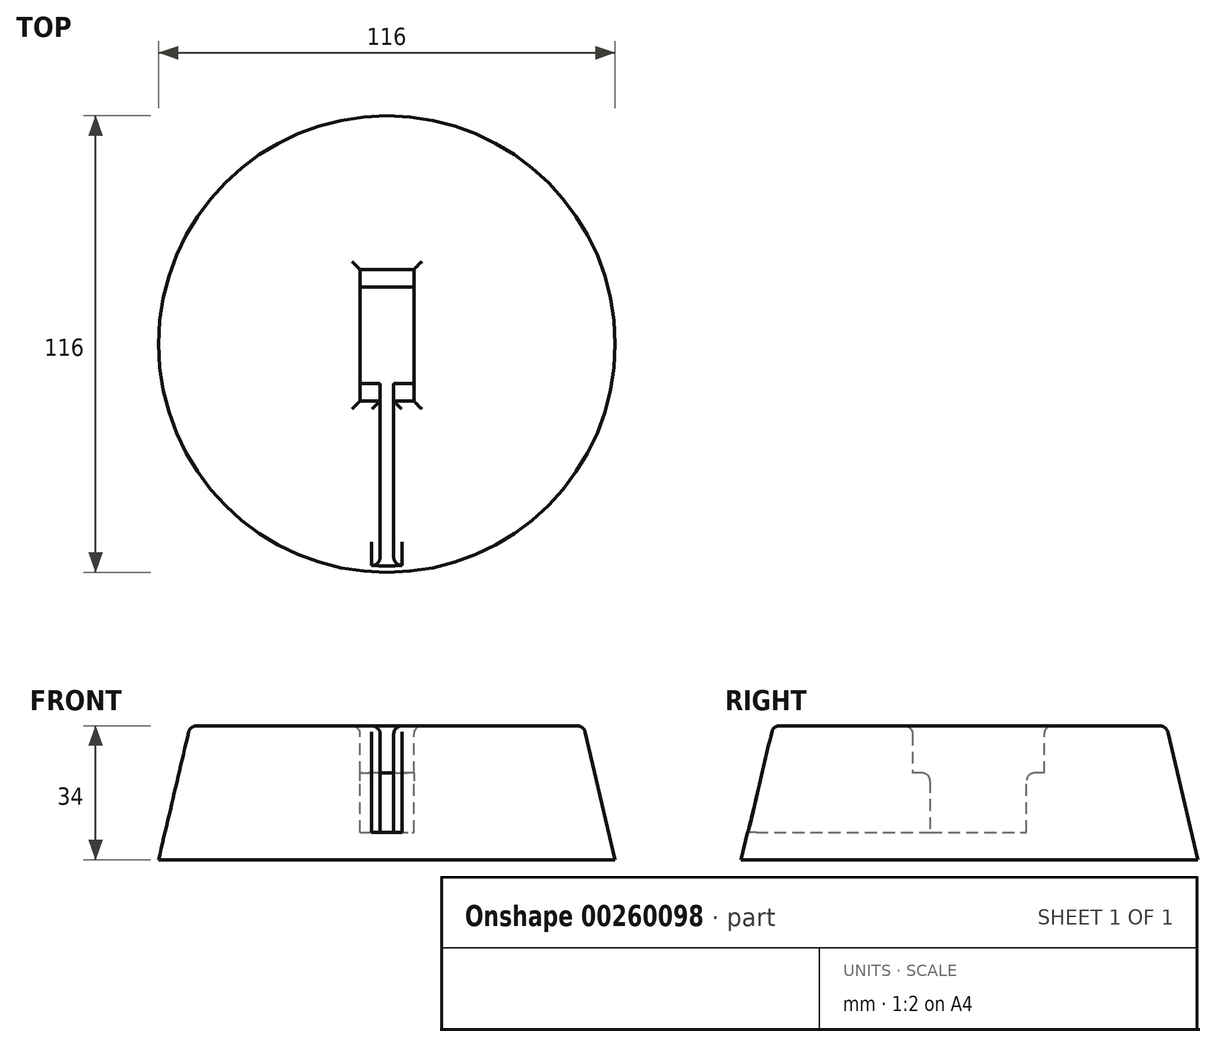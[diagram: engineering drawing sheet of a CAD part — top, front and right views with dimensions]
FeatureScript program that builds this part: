
annotation { "Feature Type Name" : "Feature", "Feature Type Description" : "" }
export const myFeature = defineFeature(function(context is Context, id is Id, definition is map)
    precondition{}
    {
        {
            var Q0;
            Q0=qCreatedBy(makeId("Top.planeOp"),FACE);
            var sketch = newSketch(context, id + "F0", { "sketchPlane" : qUnion([Q0])});
            skCircle(sketch, "E0", {"center": v(0, 0) * mm, "radius": 50 * mm});
            skSolve(sketch);
        }
        {
            var Q0;
            Q0 = qSketchRegion(id + "F0", true);
            extrude(context, id + "F1", {"entities" : qUnion([Q0]), "depth" : 34 * mm});
        }
        {
            var Q0;
            Q0=makeQuery(id+"F1.opExtrude","CAP_FACE",FACE,{"disambiguationData":[OSD([sQuery(id+"F0.wireOp",EDGE,"E0")])],"isStart":true});
            var sketch = newSketch(context, id + "F2", { "sketchPlane" : qUnion([Q0])});
            skCircle(sketch, "E1.0", {"center": v(0, 0) * mm, "radius": 58 * mm});
            skSolve(sketch);
        }
        {
            var Q0;
            Q0=makeQuery(id+"F1.opExtrude","CAP_FACE",FACE,{"disambiguationData":[OSD([sQuery(id+"F0.wireOp",EDGE,"E0")])],"isStart":false});
            var sketch = newSketch(context, id + "F3", { "sketchPlane" : qUnion([Q0])});
            skCircle(sketch, "E2.0.0", {"center": v(0, 0) * mm, "radius": 50 * mm});
            skSolve(sketch);
        }
        {
            var Q1;
            Q1=makeQuery(id+"F3.imprint","IMPRINT",FACE,{"disambiguationData":[TD([[makeQuery(id+"F3.imprint","IMPRINT",EDGE,{"derivedFrom":sQuery(id+"F3.wireOp",EDGE,"E2.0.0")}),1.0]])]});
            var Q2;
            Q2 = qSketchRegion(id + "F2", true);
            loft(context, id + "F4", {"operationType" : NewBodyOperationType.ADD, "sheetProfilesArray" : [{ "sheetProfileEntities" : qUnion([Q1]) }, { "sheetProfileEntities" : qUnion([Q2]) }]});
        }
        {
            var Q0;
            Q0=makeQuery(id+"F1.opExtrude","CAP_FACE",FACE,{"disambiguationData":[OSD([sQuery(id+"F0.wireOp",EDGE,"E0")])],"isStart":false});
            var sketch = newSketch(context, id + "F5", { "sketchPlane" : qUnion([Q0])});
            skLineSegment(sketch, "E3.bottom", {"start": v(-6.87, -10) * mm, "end": v(6.88, -10) * mm});
            skLineSegment(sketch, "E3.top", {"start": v(-6.88, 14.5) * mm, "end": v(6.87, 14.5) * mm});
            skLineSegment(sketch, "E3.left", {"start": v(-6.87, -10) * mm, "end": v(-6.88, 14.5) * mm});
            skLineSegment(sketch, "E3.right", {"start": v(6.88, -10) * mm, "end": v(6.87, 14.5) * mm});
            skSolve(sketch);
        }
        {
            var Q0;
            Q0 = qSketchRegion(id + "F5", true);
            extrude(context, id + "F6", {"entities" : qUnion([Q0]), "operationType" : NewBodyOperationType.REMOVE, "oppositeDirection" : true, "depth" : 27 * mm});
        }
        {
            var Q0;
            Q0=makeQuery(id+"F1.opExtrude","CAP_FACE",FACE,{"disambiguationData":[OSD([sQuery(id+"F0.wireOp",EDGE,"E0")])],"isStart":false});
            var sketch = newSketch(context, id + "F7", { "sketchPlane" : qUnion([Q0])});
            skPoint(sketch, "E4.oppositeSnap0", {"position": v(6.88, 2.25) * mm});
            skLineSegment(sketch, "E4.bottom", {"start": v(-6.88, 19) * mm, "end": v(6.88, 19) * mm});
            skLineSegment(sketch, "E4.top", {"start": v(-6.87, -14.5) * mm, "end": v(6.88, -14.5) * mm});
            skLineSegment(sketch, "E4.left", {"start": v(-6.88, 19) * mm, "end": v(-6.87, -14.5) * mm});
            skLineSegment(sketch, "E4.right", {"start": v(6.88, 19) * mm, "end": v(6.88, -14.5) * mm});
            skSolve(sketch);
        }
        {
            var Q0;
            Q0 = qSketchRegion(id + "F7", true);
            extrude(context, id + "F8", {"entities" : qUnion([Q0]), "operationType" : NewBodyOperationType.REMOVE, "oppositeDirection" : true, "depth" : 12 * mm});
        }
        {
            var Q0;
            Q0=makeQuery(id+"F1.opExtrude","CAP_FACE",FACE,{"disambiguationData":[OSD([sQuery(id+"F0.wireOp",EDGE,"E0")])],"isStart":false});
            var sketch = newSketch(context, id + "F9", { "sketchPlane" : qUnion([Q0])});
            skLineSegment(sketch, "E5.bottom", {"start": v(-1.75, -6.6) * mm, "end": v(1.75, -6.6) * mm});
            skLineSegment(sketch, "E5.top", {"start": v(-1.75, -69.31) * mm, "end": v(1.75, -69.31) * mm});
            skLineSegment(sketch, "E5.left", {"start": v(-1.75, -6.6) * mm, "end": v(-1.75, -69.31) * mm});
            skLineSegment(sketch, "E5.right", {"start": v(1.75, -6.6) * mm, "end": v(1.75, -69.31) * mm});
            skLineSegment(sketch, "E6", {"start": v(0, 50) * mm, "end": v(0, -50) * mm, "construction": true});
            skSolve(sketch);
        }
        {
            var Q0;
            Q0 = qSketchRegion(id + "F9", true);
            var Q1;
            Q1=makeQuery(id+"F6.boolean.opBoolean","COPY",FACE,{"derivedFrom":makeQuery(id+"F6.opExtrude","CAP_FACE",FACE,{"disambiguationData":[OSD([sQuery(id+"F5.wireOp",EDGE,"E3.bottom"),sQuery(id+"F5.wireOp",EDGE,"E3.top"),sQuery(id+"F5.wireOp",EDGE,"E3.left"),sQuery(id+"F5.wireOp",EDGE,"E3.right")])],"isStart":false})});
            extrude(context, id + "F10", {"entities" : qUnion([Q0]), "operationType" : NewBodyOperationType.REMOVE, "endBound" : BoundingType.UP_TO_SURFACE, "oppositeDirection" : true, "endBoundEntityFace" : qUnion([Q1]), "depth" : 25 * mm});
        }
        {
            var Q0;
            Q0=makeQuery(id+"F8.boolean.opBoolean","COPY",EDGE,{"derivedFrom":makeQuery(id+"F8.opExtrude","CAP_EDGE",EDGE,{"disambiguationData":[OSD([sQuery(id+"F7.wireOp",EDGE,"HFsGuh67-IHWy-x5wL-GzuI-69m3aBAS32or.bottom")])],"isStart":true})});
            var Q1;
            Q1=makeQuery(id+"F8.boolean.opBoolean","MERGE",EDGE,{"derivedFrom":[makeQuery(id+"F6.boolean.opBoolean","COPY",EDGE,{"derivedFrom":makeQuery(id+"F6.opExtrude","CAP_EDGE",EDGE,{"disambiguationData":[OSD([sQuery(id+"F5.wireOp",EDGE,"IrSC4I5D-AX9H-FrcX-Zehj-UdF8axFLpcCN.left")])],"isStart":true})}),makeQuery(id+"F8.opExtrude","CAP_EDGE",EDGE,{"disambiguationData":[OSD([sQuery(id+"F7.wireOp",EDGE,"HFsGuh67-IHWy-x5wL-GzuI-69m3aBAS32or.left")])],"isStart":true})]});
            var Q2;
            Q2=makeQuery(id+"F8.boolean.opBoolean","MERGE",EDGE,{"derivedFrom":[makeQuery(id+"F6.boolean.opBoolean","COPY",EDGE,{"derivedFrom":makeQuery(id+"F6.opExtrude","CAP_EDGE",EDGE,{"disambiguationData":[OSD([sQuery(id+"F5.wireOp",EDGE,"IrSC4I5D-AX9H-FrcX-Zehj-UdF8axFLpcCN.right")])],"isStart":true})}),makeQuery(id+"F8.opExtrude","CAP_EDGE",EDGE,{"disambiguationData":[OSD([sQuery(id+"F7.wireOp",EDGE,"HFsGuh67-IHWy-x5wL-GzuI-69m3aBAS32or.right")])],"isStart":true})]});
            var Q3;
            {var subQ0=sQuery(id+"F7.wireOp",EDGE,"HFsGuh67-IHWy-x5wL-GzuI-69m3aBAS32or.top");Q3=makeQuery(id+"F10.boolean.opBoolean","SPLIT",EDGE,{"disambiguationData":[TD([makeQuery(id+"F6.boolean.opBoolean","COPY",FACE,{"derivedFrom":makeQuery(id+"F6.opExtrude","SWEPT_FACE",FACE,{"disambiguationData":[OSD([sQuery(id+"F5.wireOp",EDGE,"IrSC4I5D-AX9H-FrcX-Zehj-UdF8axFLpcCN.right")])]})})])],"derivedFrom":makeQuery(id+"F8.boolean.opBoolean","COPY",EDGE,{"derivedFrom":makeQuery(id+"F8.opExtrude","CAP_EDGE",EDGE,{"disambiguationData":[OSD([subQ0])],"isStart":true})})});}
            var Q4;
            Q4=makeQuery(id+"F1.opExtrude","CAP_FACE",FACE,{"disambiguationData":[OSD([sQuery(id+"F0.wireOp",EDGE,"E0")])],"isStart":false});
            var Q5;
            Q5=makeQuery(id+"F10.boolean.opBoolean","INTERSECT",EDGE,{"derivedFrom":[makeQuery(id+"F4.opLoft","SWEPT_FACE",FACE,{"disambiguationData":[OSD([sQuery(id+"F2.wireOp",EDGE,"E1.0"),sQuery(id+"F3.wireOp",EDGE,"E2.0.0")])]}),makeQuery(id+"F10.opExtrude","SWEPT_FACE",FACE,{"disambiguationData":[OSD([sQuery(id+"F9.wireOp",EDGE,"E5.left")])]})]});
            var Q6;
            Q6=makeQuery(id+"F10.boolean.opBoolean","INTERSECT",EDGE,{"derivedFrom":[makeQuery(id+"F4.opLoft","SWEPT_FACE",FACE,{"disambiguationData":[OSD([sQuery(id+"F2.wireOp",EDGE,"E1.0"),sQuery(id+"F3.wireOp",EDGE,"E2.0.0")])]}),makeQuery(id+"F10.opExtrude","SWEPT_FACE",FACE,{"disambiguationData":[OSD([sQuery(id+"F9.wireOp",EDGE,"E5.right")])]})]});
            var Q7;
            Q7=makeQuery(id+"F10.boolean.opBoolean","INTERSECT",EDGE,{"derivedFrom":[makeQuery(id+"F4.opLoft","SWEPT_FACE",FACE,{"disambiguationData":[OSD([sQuery(id+"F2.wireOp",EDGE,"E1.0"),sQuery(id+"F3.wireOp",EDGE,"E2.0.0")])]}),makeQuery(id+"F10.opExtrude","CAP_FACE",FACE,{"disambiguationData":[OSD([sQuery(id+"F5.wireOp",EDGE,"IrSC4I5D-AX9H-FrcX-Zehj-UdF8axFLpcCN.bottom"),sQuery(id+"F5.wireOp",EDGE,"IrSC4I5D-AX9H-FrcX-Zehj-UdF8axFLpcCN.top"),sQuery(id+"F5.wireOp",EDGE,"IrSC4I5D-AX9H-FrcX-Zehj-UdF8axFLpcCN.left"),sQuery(id+"F5.wireOp",EDGE,"IrSC4I5D-AX9H-FrcX-Zehj-UdF8axFLpcCN.right")])],"isStart":false})]});
            var Q8;
            {var subQ0=sQuery(id+"F7.wireOp",EDGE,"HFsGuh67-IHWy-x5wL-GzuI-69m3aBAS32or.top");var subQ1=makeQuery(id+"F6.boolean.opBoolean","COPY",FACE,{"derivedFrom":makeQuery(id+"F6.opExtrude","SWEPT_FACE",FACE,{"disambiguationData":[OSD([sQuery(id+"F5.wireOp",EDGE,"IrSC4I5D-AX9H-FrcX-Zehj-UdF8axFLpcCN.right")])]})});var subQ2=makeQuery(id+"F6.boolean.opBoolean","COPY",FACE,{"derivedFrom":makeQuery(id+"F6.opExtrude","SWEPT_FACE",FACE,{"disambiguationData":[OSD([sQuery(id+"F5.wireOp",EDGE,"IrSC4I5D-AX9H-FrcX-Zehj-UdF8axFLpcCN.top")])]})});var subQ3=sQuery(id+"F7.wireOp",EDGE,"HFsGuh67-IHWy-x5wL-GzuI-69m3aBAS32or.left");var subQ4=sQuery(id+"F7.wireOp",EDGE,"HFsGuh67-IHWy-x5wL-GzuI-69m3aBAS32or.right");var subQ6=makeQuery(id+"F8.opExtrude","CAP_FACE",FACE,{"disambiguationData":[OSD([sQuery(id+"F7.wireOp",EDGE,"HFsGuh67-IHWy-x5wL-GzuI-69m3aBAS32or.bottom"),subQ0,subQ3,subQ4])],"isStart":false});Q8=makeQuery(id+"F10.boolean.opBoolean","SPLIT",EDGE,{"disambiguationData":[TD([subQ1])],"derivedFrom":makeQuery(id+"F8.boolean.opBoolean","INTERSECT",EDGE,{"derivedFrom":[subQ2,subQ6]})});}
            var Q9;
            {var subQ0=sQuery(id+"F7.wireOp",EDGE,"HFsGuh67-IHWy-x5wL-GzuI-69m3aBAS32or.top");var subQ1=makeQuery(id+"F6.boolean.opBoolean","COPY",FACE,{"derivedFrom":makeQuery(id+"F6.opExtrude","SWEPT_FACE",FACE,{"disambiguationData":[OSD([sQuery(id+"F5.wireOp",EDGE,"IrSC4I5D-AX9H-FrcX-Zehj-UdF8axFLpcCN.left")])]})});var subQ2=makeQuery(id+"F6.boolean.opBoolean","COPY",FACE,{"derivedFrom":makeQuery(id+"F6.opExtrude","SWEPT_FACE",FACE,{"disambiguationData":[OSD([sQuery(id+"F5.wireOp",EDGE,"IrSC4I5D-AX9H-FrcX-Zehj-UdF8axFLpcCN.top")])]})});var subQ3=sQuery(id+"F7.wireOp",EDGE,"HFsGuh67-IHWy-x5wL-GzuI-69m3aBAS32or.left");var subQ5=sQuery(id+"F7.wireOp",EDGE,"HFsGuh67-IHWy-x5wL-GzuI-69m3aBAS32or.right");var subQ6=makeQuery(id+"F8.opExtrude","CAP_FACE",FACE,{"disambiguationData":[OSD([sQuery(id+"F7.wireOp",EDGE,"HFsGuh67-IHWy-x5wL-GzuI-69m3aBAS32or.bottom"),subQ0,subQ3,subQ5])],"isStart":false});Q9=makeQuery(id+"F10.boolean.opBoolean","SPLIT",EDGE,{"disambiguationData":[TD([subQ1])],"derivedFrom":makeQuery(id+"F8.boolean.opBoolean","INTERSECT",EDGE,{"derivedFrom":[subQ2,subQ6]})});}
            var Q10;
            Q10=makeQuery(id+"F8.boolean.opBoolean","INTERSECT",EDGE,{"derivedFrom":[makeQuery(id+"F6.boolean.opBoolean","COPY",FACE,{"derivedFrom":makeQuery(id+"F6.opExtrude","SWEPT_FACE",FACE,{"disambiguationData":[OSD([sQuery(id+"F5.wireOp",EDGE,"IrSC4I5D-AX9H-FrcX-Zehj-UdF8axFLpcCN.bottom")])]})}),makeQuery(id+"F8.opExtrude","CAP_FACE",FACE,{"disambiguationData":[OSD([sQuery(id+"F7.wireOp",EDGE,"HFsGuh67-IHWy-x5wL-GzuI-69m3aBAS32or.bottom"),sQuery(id+"F7.wireOp",EDGE,"HFsGuh67-IHWy-x5wL-GzuI-69m3aBAS32or.top"),sQuery(id+"F7.wireOp",EDGE,"HFsGuh67-IHWy-x5wL-GzuI-69m3aBAS32or.left"),sQuery(id+"F7.wireOp",EDGE,"HFsGuh67-IHWy-x5wL-GzuI-69m3aBAS32or.right")])],"isStart":false})]});
            var Q11;
            Q11=makeQuery(id+"F10.boolean.opBoolean","INTERSECT",EDGE,{"derivedFrom":[makeQuery(id+"F6.boolean.opBoolean","COPY",FACE,{"derivedFrom":makeQuery(id+"F6.opExtrude","SWEPT_FACE",FACE,{"disambiguationData":[OSD([sQuery(id+"F5.wireOp",EDGE,"IrSC4I5D-AX9H-FrcX-Zehj-UdF8axFLpcCN.top")])]})}),makeQuery(id+"F10.opExtrude","SWEPT_FACE",FACE,{"disambiguationData":[OSD([sQuery(id+"F9.wireOp",EDGE,"E5.left")])]})]});
            var Q12;
            {var subQ0=sQuery(id+"F7.wireOp",EDGE,"HFsGuh67-IHWy-x5wL-GzuI-69m3aBAS32or.top");var subQ1=sQuery(id+"F7.wireOp",EDGE,"HFsGuh67-IHWy-x5wL-GzuI-69m3aBAS32or.left");var subQ2=sQuery(id+"F7.wireOp",EDGE,"HFsGuh67-IHWy-x5wL-GzuI-69m3aBAS32or.right");Q12=makeQuery(id+"F10.boolean.opBoolean","INTERSECT",EDGE,{"derivedFrom":[makeQuery(id+"F8.boolean.opBoolean","COPY",FACE,{"disambiguationData":[TD([makeQuery(id+"F6.boolean.opBoolean","COPY",FACE,{"derivedFrom":makeQuery(id+"F6.opExtrude","SWEPT_FACE",FACE,{"disambiguationData":[OSD([sQuery(id+"F5.wireOp",EDGE,"IrSC4I5D-AX9H-FrcX-Zehj-UdF8axFLpcCN.top")])]})})])],"derivedFrom":makeQuery(id+"F8.opExtrude","CAP_FACE",FACE,{"disambiguationData":[OSD([sQuery(id+"F7.wireOp",EDGE,"HFsGuh67-IHWy-x5wL-GzuI-69m3aBAS32or.bottom"),subQ0,subQ1,subQ2])],"isStart":false})}),makeQuery(id+"F10.opExtrude","SWEPT_FACE",FACE,{"disambiguationData":[OSD([sQuery(id+"F9.wireOp",EDGE,"E5.left")])]})]});}
            var Q13;
            Q13=makeQuery(id+"F10.boolean.opBoolean","INTERSECT",EDGE,{"derivedFrom":[makeQuery(id+"F8.boolean.opBoolean","COPY",FACE,{"derivedFrom":makeQuery(id+"F8.opExtrude","SWEPT_FACE",FACE,{"disambiguationData":[OSD([sQuery(id+"F7.wireOp",EDGE,"HFsGuh67-IHWy-x5wL-GzuI-69m3aBAS32or.top")])]})}),makeQuery(id+"F10.opExtrude","SWEPT_FACE",FACE,{"disambiguationData":[OSD([sQuery(id+"F9.wireOp",EDGE,"E5.left")])]})]});
            var Q14;
            Q14=makeQuery(id+"F10.boolean.opBoolean","INTERSECT",EDGE,{"derivedFrom":[makeQuery(id+"F6.boolean.opBoolean","COPY",FACE,{"derivedFrom":makeQuery(id+"F6.opExtrude","SWEPT_FACE",FACE,{"disambiguationData":[OSD([sQuery(id+"F5.wireOp",EDGE,"IrSC4I5D-AX9H-FrcX-Zehj-UdF8axFLpcCN.top")])]})}),makeQuery(id+"F10.opExtrude","SWEPT_FACE",FACE,{"disambiguationData":[OSD([sQuery(id+"F9.wireOp",EDGE,"E5.right")])]})]});
            var Q15;
            {var subQ0=sQuery(id+"F7.wireOp",EDGE,"HFsGuh67-IHWy-x5wL-GzuI-69m3aBAS32or.top");var subQ1=sQuery(id+"F7.wireOp",EDGE,"HFsGuh67-IHWy-x5wL-GzuI-69m3aBAS32or.left");var subQ2=sQuery(id+"F7.wireOp",EDGE,"HFsGuh67-IHWy-x5wL-GzuI-69m3aBAS32or.right");Q15=makeQuery(id+"F10.boolean.opBoolean","INTERSECT",EDGE,{"derivedFrom":[makeQuery(id+"F8.boolean.opBoolean","COPY",FACE,{"disambiguationData":[TD([makeQuery(id+"F6.boolean.opBoolean","COPY",FACE,{"derivedFrom":makeQuery(id+"F6.opExtrude","SWEPT_FACE",FACE,{"disambiguationData":[OSD([sQuery(id+"F5.wireOp",EDGE,"IrSC4I5D-AX9H-FrcX-Zehj-UdF8axFLpcCN.top")])]})})])],"derivedFrom":makeQuery(id+"F8.opExtrude","CAP_FACE",FACE,{"disambiguationData":[OSD([sQuery(id+"F7.wireOp",EDGE,"HFsGuh67-IHWy-x5wL-GzuI-69m3aBAS32or.bottom"),subQ0,subQ1,subQ2])],"isStart":false})}),makeQuery(id+"F10.opExtrude","SWEPT_FACE",FACE,{"disambiguationData":[OSD([sQuery(id+"F9.wireOp",EDGE,"E5.right")])]})]});}
            var Q16;
            Q16=makeQuery(id+"F10.boolean.opBoolean","INTERSECT",EDGE,{"derivedFrom":[makeQuery(id+"F8.boolean.opBoolean","COPY",FACE,{"derivedFrom":makeQuery(id+"F8.opExtrude","SWEPT_FACE",FACE,{"disambiguationData":[OSD([sQuery(id+"F7.wireOp",EDGE,"HFsGuh67-IHWy-x5wL-GzuI-69m3aBAS32or.top")])]})}),makeQuery(id+"F10.opExtrude","SWEPT_FACE",FACE,{"disambiguationData":[OSD([sQuery(id+"F9.wireOp",EDGE,"E5.right")])]})]});
            var Q17;
            {var subQ0=sQuery(id+"F7.wireOp",EDGE,"E4.top");var subQ1=makeQuery(id+"F6.boolean.opBoolean","COPY",FACE,{"derivedFrom":makeQuery(id+"F6.opExtrude","SWEPT_FACE",FACE,{"disambiguationData":[OSD([sQuery(id+"F5.wireOp",EDGE,"E3.left")])]})});var subQ2=makeQuery(id+"F6.boolean.opBoolean","COPY",FACE,{"derivedFrom":makeQuery(id+"F6.opExtrude","SWEPT_FACE",FACE,{"disambiguationData":[OSD([sQuery(id+"F5.wireOp",EDGE,"E3.bottom")])]})});var subQ3=sQuery(id+"F7.wireOp",EDGE,"E4.left");var subQ5=sQuery(id+"F7.wireOp",EDGE,"E4.right");var subQ6=makeQuery(id+"F8.opExtrude","CAP_FACE",FACE,{"disambiguationData":[OSD([sQuery(id+"F7.wireOp",EDGE,"E4.bottom"),subQ0,subQ3,subQ5])],"isStart":false});Q17=makeQuery(id+"F10.boolean.opBoolean","SPLIT",EDGE,{"disambiguationData":[TD([subQ1])],"derivedFrom":makeQuery(id+"F8.boolean.opBoolean","INTERSECT",EDGE,{"derivedFrom":[subQ2,subQ6]})});}
            var Q18;
            {var subQ0=sQuery(id+"F7.wireOp",EDGE,"E4.top");var subQ1=makeQuery(id+"F6.boolean.opBoolean","COPY",FACE,{"derivedFrom":makeQuery(id+"F6.opExtrude","SWEPT_FACE",FACE,{"disambiguationData":[OSD([sQuery(id+"F5.wireOp",EDGE,"E3.right")])]})});var subQ2=makeQuery(id+"F6.boolean.opBoolean","COPY",FACE,{"derivedFrom":makeQuery(id+"F6.opExtrude","SWEPT_FACE",FACE,{"disambiguationData":[OSD([sQuery(id+"F5.wireOp",EDGE,"E3.bottom")])]})});var subQ3=sQuery(id+"F7.wireOp",EDGE,"E4.left");var subQ4=sQuery(id+"F7.wireOp",EDGE,"E4.right");var subQ6=makeQuery(id+"F8.opExtrude","CAP_FACE",FACE,{"disambiguationData":[OSD([sQuery(id+"F7.wireOp",EDGE,"E4.bottom"),subQ0,subQ3,subQ4])],"isStart":false});Q18=makeQuery(id+"F10.boolean.opBoolean","SPLIT",EDGE,{"disambiguationData":[TD([subQ1])],"derivedFrom":makeQuery(id+"F8.boolean.opBoolean","INTERSECT",EDGE,{"derivedFrom":[subQ2,subQ6]})});}
            var Q19;
            Q19=makeQuery(id+"F8.boolean.opBoolean","INTERSECT",EDGE,{"derivedFrom":[makeQuery(id+"F6.boolean.opBoolean","COPY",FACE,{"derivedFrom":makeQuery(id+"F6.opExtrude","SWEPT_FACE",FACE,{"disambiguationData":[OSD([sQuery(id+"F5.wireOp",EDGE,"E3.top")])]})}),makeQuery(id+"F8.opExtrude","CAP_FACE",FACE,{"disambiguationData":[OSD([sQuery(id+"F7.wireOp",EDGE,"E4.bottom"),sQuery(id+"F7.wireOp",EDGE,"E4.top"),sQuery(id+"F7.wireOp",EDGE,"E4.left"),sQuery(id+"F7.wireOp",EDGE,"E4.right")])],"isStart":false})]});
            fillet(context, id + "F11", {"entities" : qUnion([Q0, Q1, Q2, Q3, Q4, Q5, Q6, Q7, Q8, Q9, Q10, Q11, Q12, Q13, Q14, Q15, Q16, Q17, Q18, Q19]), "radius" : 2 * mm, "tangentPropagation" : true, "allowEdgeOverflow" : false});
        }
    });
